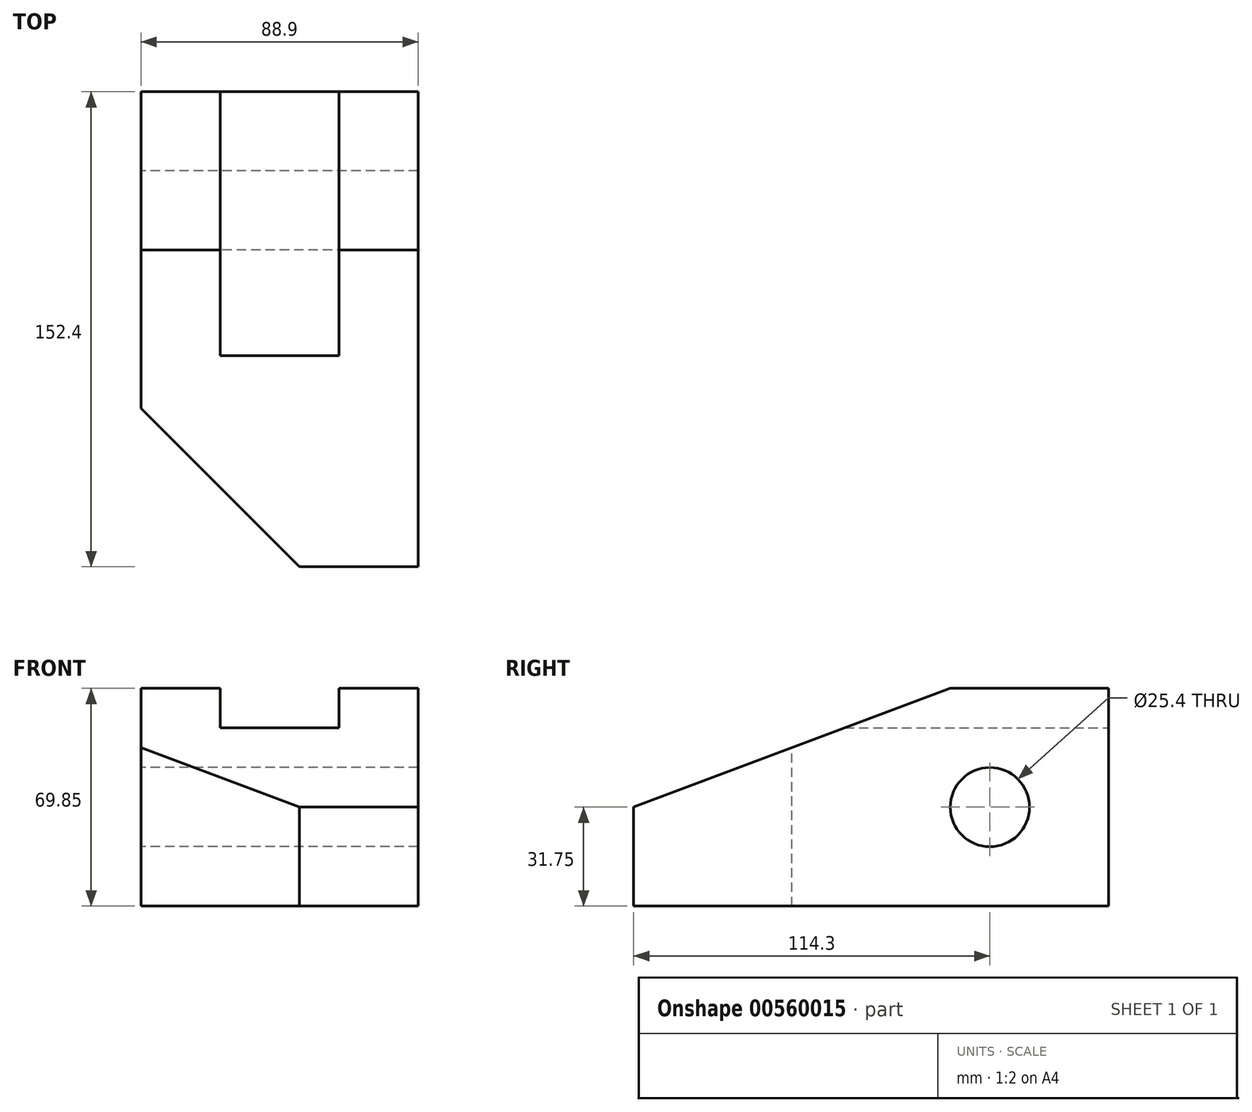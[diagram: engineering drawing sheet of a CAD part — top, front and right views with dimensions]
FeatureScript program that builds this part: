
annotation { "Feature Type Name" : "Feature", "Feature Type Description" : "" }
export const myFeature = defineFeature(function(context is Context, id is Id, definition is map)
    precondition{}
    {
        {
            var Q0;
            Q0=qCreatedBy(makeId("Right.planeOp"),FACE);
            var sketch = newSketch(context, id + "F0", { "sketchPlane" : qUnion([Q0])});
            skLineSegment(sketch, "E0", {"start": v(0, 0) * mm, "end": v(-101.6, 0) * mm});
            skLineSegment(sketch, "E1", {"start": v(-50.8, 69.85) * mm, "end": v(0, 69.85) * mm});
            skLineSegment(sketch, "E2", {"start": v(0, 69.85) * mm, "end": v(0, 0) * mm});
            skCircle(sketch, "E3", {"center": v(-38.1, 31.75) * mm, "radius": 12.7 * mm});
            skLineSegment(sketch, "E4", {"start": v(-38.1, 31.75) * mm, "end": v(-38.1, 44.45) * mm, "construction": true});
            skLineSegment(sketch, "E5", {"start": v(-101.6, 0) * mm, "end": v(-101.6, 50.8) * mm});
            skLineSegment(sketch, "E6", {"start": v(-101.6, 50.8) * mm, "end": v(-50.8, 69.85) * mm});
            skSolve(sketch);
        }
        {
            var Q0;
            Q0 = qSketchRegion(id + "F0", true);
            extrude(context, id + "F1", {"entities" : qUnion([Q0]), "depth" : 88.9 * mm, "offsetDistance" : 25.4 * mm});
        }
        {
            var Q0;
            Q0=makeQuery(id+"F1.opExtrude","SWEPT_FACE",FACE,{"disambiguationData":[OSD([sQuery(id+"F0.wireOp",EDGE,"E2")])]});
            var sketch = newSketch(context, id + "F2", { "sketchPlane" : qUnion([Q0])});
            skLineSegment(sketch, "E7", {"start": v(0, 69.85) * mm, "end": v(-25.4, 69.85) * mm, "construction": true});
            skLineSegment(sketch, "E8.bottom", {"start": v(-25.4, 69.85) * mm, "end": v(-63.5, 69.85) * mm});
            skLineSegment(sketch, "E8.top", {"start": v(-25.4, 57.15) * mm, "end": v(-63.5, 57.15) * mm});
            skLineSegment(sketch, "E8.left", {"start": v(-25.4, 69.85) * mm, "end": v(-25.4, 57.15) * mm});
            skLineSegment(sketch, "E8.right", {"start": v(-63.5, 69.85) * mm, "end": v(-63.5, 57.15) * mm});
            skSolve(sketch);
        }
        {
            var Q0;
            Q0 = qSketchRegion(id + "F2", true);
            extrude(context, id + "F3", {"entities" : qUnion([Q0]), "operationType" : NewBodyOperationType.REMOVE, "oppositeDirection" : true, "depth" : 101.6 * mm, "offsetDistance" : 25.4 * mm});
        }
        {
            var Q0;
            Q0=makeQuery(id+"F1.opExtrude","SWEPT_FACE",FACE,{"disambiguationData":[OSD([sQuery(id+"F0.wireOp",EDGE,"E5")])]});
            extrude(context, id + "F4", {"entities" : qUnion([Q0]), "operationType" : NewBodyOperationType.ADD, "depth" : 50.8 * mm, "offsetDistance" : 25.4 * mm});
        }
        {
            var Q0;
            Q0=makeQuery(id+"F4.opExtrude","SWEPT_FACE",FACE,{"disambiguationData":[OSD([sQuery(id+"F0.wireOp",EDGE,"E5"),sQuery(id+"F0.wireOp",EDGE,"E6")])]});
            var sketch = newSketch(context, id + "F5", { "sketchPlane" : qUnion([Q0])});
            skLineSegment(sketch, "E9", {"start": v(88.9, -152.4) * mm, "end": v(50.8, -152.4) * mm, "construction": true});
            skLineSegment(sketch, "E10", {"start": v(50.8, -152.4) * mm, "end": v(0, -101.6) * mm});
            skSolve(sketch);
        }
        {
            var Q0;
            Q0 = qSketchRegion(id + "F5", true);
            var Q1;
            {var subQ0=sQuery(id+"F5.wireOp",EDGE,"E10");Q1=makeQuery(id+"F5.imprint","IMPRINT",FACE,{"disambiguationData":[TD([[makeQuery(id+"F5.imprint","IMPRINT",EDGE,{"derivedFrom":subQ0}),1.0]])]});}
            extrude(context, id + "F6", {"entities" : qUnion([Q0, Q1]), "operationType" : NewBodyOperationType.REMOVE, "endBound" : BoundingType.THROUGH_ALL, "oppositeDirection" : true, "depth" : 25.4 * mm, "offsetDistance" : 25.4 * mm});
        }
        {
            var Q0;
            {var subQ0=sQuery(id+"F0.wireOp",EDGE,"E5");Q0=makeQuery(id+"F4.boolean.opBoolean","MERGE",FACE,{"derivedFrom":[makeQuery(id+"F1.opExtrude","CAP_FACE",FACE,{"disambiguationData":[OSD([sQuery(id+"F0.wireOp",EDGE,"E0"),sQuery(id+"F0.wireOp",EDGE,"E1"),sQuery(id+"F0.wireOp",EDGE,"E2"),sQuery(id+"F0.wireOp",EDGE,"E3"),subQ0,sQuery(id+"F0.wireOp",EDGE,"E6")])],"isStart":false}),makeQuery(id+"F4.opExtrude","SWEPT_FACE",FACE,{"disambiguationData":[OSD([subQ0]),TDD([makeQuery(id+"F1.opExtrude","CAP_EDGE",EDGE,{"disambiguationData":[OSD([subQ0])],"isStart":false})])]})]});}
            var sketch = newSketch(context, id + "F7", { "sketchPlane" : qUnion([Q0])});
            skLineSegment(sketch, "E11", {"start": v(-152.4, 0) * mm, "end": v(-152.4, 31.75) * mm, "construction": true});
            skLineSegment(sketch, "E12", {"start": v(-101.6, 50.8) * mm, "end": v(-152.4, 31.75) * mm});
            skSolve(sketch);
        }
        {
            var Q0;
            Q0 = qSketchRegion(id + "F7", true);
            var Q1;
            {var subQ0=sQuery(id+"F7.wireOp",EDGE,"E12");Q1=makeQuery(id+"F7.imprint","IMPRINT",FACE,{"disambiguationData":[TD([[makeQuery(id+"F7.imprint","IMPRINT",EDGE,{"derivedFrom":subQ0}),-1.0]])]});}
            extrude(context, id + "F8", {"entities" : qUnion([Q0, Q1]), "operationType" : NewBodyOperationType.REMOVE, "endBound" : BoundingType.THROUGH_ALL, "oppositeDirection" : true, "depth" : 25.4 * mm, "offsetDistance" : 25.4 * mm});
        }
    });
